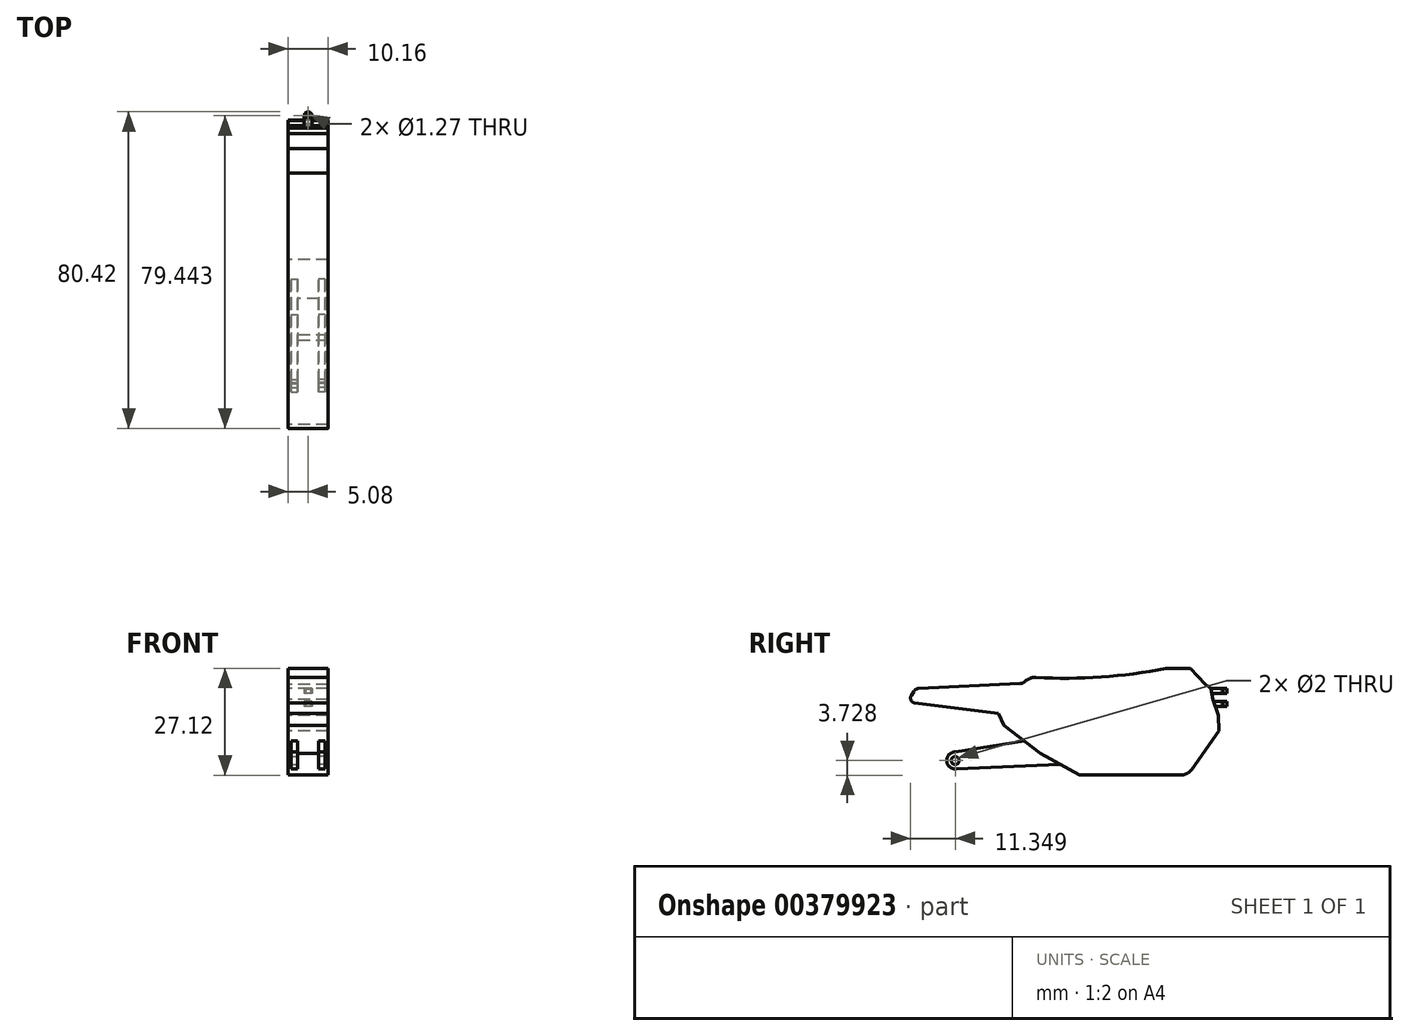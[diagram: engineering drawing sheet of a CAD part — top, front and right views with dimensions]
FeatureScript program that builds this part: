
annotation { "Feature Type Name" : "Feature", "Feature Type Description" : "" }
export const myFeature = defineFeature(function(context is Context, id is Id, definition is map)
    precondition{}
    {
        {
            var Q0;
            Q0=qCreatedBy(makeId("Right.planeOp"),FACE);
            var sketch = newSketch(context, id + "F0", { "sketchPlane" : qUnion([Q0])});
            skLineSegment(sketch, "E0", {"start": v(0.03, 4.05) * mm, "end": v(-1.34, 8.22) * mm});
            skLineSegment(sketch, "E1", {"start": v(-3.3, 12.01) * mm, "end": v(-7.13, 16.04) * mm});
            skLineSegment(sketch, "E2", {"start": v(-7.13, 16.04) * mm, "end": v(-13.37, 16.04) * mm});
            skLineSegment(sketch, "E3", {"start": v(-49.12, 12.73) * mm, "end": v(-49.2, 12.66) * mm});
            skLineSegment(sketch, "E4", {"start": v(-50.36, 12.17) * mm, "end": v(-76.22, 10.91) * mm});
            skLineSegment(sketch, "E5", {"start": v(-77.36, 10.24) * mm, "end": v(-78.02, 9.16) * mm});
            skLineSegment(sketch, "E6", {"start": v(-6.72, -9.55) * mm, "end": v(0.09, 0.2) * mm});
            skLineSegment(sketch, "E7", {"start": v(0.09, 0.2) * mm, "end": v(0.03, 4.05) * mm});
            skArc(sketch, "E8", {"start": v(-46.3, 13.76) * mm, "mid": v(-29.76, 13.87) * mm, "end": v(-13.37, 16.04) * mm});
            skPoint(sketch, "E9.visualSharp", {"position": v(-47.92, 13.86) * mm});
            skArc(sketch, "E9.filletArc", {"start": v(-46.3, 13.76) * mm, "mid": v(-47.82, 13.53) * mm, "end": v(-49.12, 12.73) * mm});
            skPoint(sketch, "E10.visualSharp", {"position": v(-78.92, 7.68) * mm});
            skArc(sketch, "E10.filletArc", {"start": v(-78.02, 9.16) * mm, "mid": v(-78.11, 8.01) * mm, "end": v(-77.24, 7.27) * mm});
            skPoint(sketch, "E11.visualSharp", {"position": v(-76.97, 10.88) * mm});
            skArc(sketch, "E11.filletArc", {"start": v(-76.22, 10.91) * mm, "mid": v(-76.88, 10.72) * mm, "end": v(-77.36, 10.24) * mm});
            skPoint(sketch, "E12.visualSharp", {"position": v(-49.69, 12.2) * mm});
            skArc(sketch, "E12.filletArc", {"start": v(-50.36, 12.17) * mm, "mid": v(-49.73, 12.31) * mm, "end": v(-49.2, 12.66) * mm});
            skPoint(sketch, "E13.visualSharp", {"position": v(-10.32, -14.7) * mm});
            skLineSegment(sketch, "E14", {"start": v(-54.53, 1.5) * mm, "end": v(-55.89, 4.57) * mm});
            skLineSegment(sketch, "E15", {"start": v(-55.89, 4.57) * mm, "end": v(-77.24, 7.27) * mm});
            skLineSegment(sketch, "E16", {"start": v(-35.32, -11.08) * mm, "end": v(-45.2, -5.51) * mm});
            skLineSegment(sketch, "E17", {"start": v(-45.2, -5.51) * mm, "end": v(-54.53, 1.5) * mm});
            skLineSegment(sketch, "E18", {"start": v(-35.32, -11.08) * mm, "end": v(-9.64, -11.08) * mm});
            skPoint(sketch, "E19.visualSharp", {"position": v(-7.79, -11.08) * mm});
            skArc(sketch, "E19.filletArc", {"start": v(-9.64, -11.08) * mm, "mid": v(-8, -10.67) * mm, "end": v(-6.72, -9.55) * mm});
            skPoint(sketch, "E20.endSnap0", {"position": v(-63.29, 11.54) * mm});
            skLineSegment(sketch, "E21", {"start": v(-49.3, -2.43) * mm, "end": v(-66.86, -5.2) * mm});
            skLineSegment(sketch, "E22", {"start": v(-66.86, -9.5) * mm, "end": v(-40.26, -8.3) * mm});
            skPoint(sketch, "E20.end.orphan", {"position": v(-63.29, -9.53) * mm});
            skPoint(sketch, "E23.end.orphan", {"position": v(-63.29, -5.99) * mm});
            skArc(sketch, "E24", {"start": v(-66.83, -5.2) * mm, "mid": v(-69.01, -7.48) * mm, "end": v(-66.58, -9.49) * mm});
            skCircle(sketch, "E25", {"center": v(-66.86, -7.35) * mm, "radius": 1 * mm});
            skLineSegment(sketch, "E26", {"start": v(-1.34, 8.22) * mm, "end": v(-1.93, 10.91) * mm});
            skLineSegment(sketch, "E27", {"start": v(-1.93, 10.91) * mm, "end": v(-3.3, 12.01) * mm});
            skPoint(sketch, "E28.orphan", {"position": v(-2.2, 10.88) * mm});
            skSolve(sketch);
        }
        {
            var Q0;
            Q0=makeQuery(id+"F0.imprint","IMPRINT",FACE,{"disambiguationData":[TD([[makeQuery(id+"F0.imprint","IMPRINT",EDGE,{"derivedFrom":sQuery(id+"F0.wireOp",EDGE,"E0")}),1.0]])]});
            extrude(context, id + "F1", {"entities" : qUnion([Q0]), "depth" : 5.08 * mm, "hasSecondDirection" : true, "secondDirectionOppositeDirection" : true, "secondDirectionDepth" : 5.08 * mm});
        }
        {
            var Q0;
            {var subQ3=sQuery(id+"F0.wireOp",EDGE,"E24");Q0=makeQuery(id+"F0.imprint","IMPRINT",FACE,{"disambiguationData":[TD([[makeQuery(id+"F0.imprint","IMPRINT",EDGE,{"derivedFrom":subQ3}),1.0]])]});}
            extrude(context, id + "F2", {"entities" : qUnion([Q0]), "depth" : 4.32 * mm, "hasSecondDirection" : true, "secondDirectionOppositeDirection" : false, "secondDirectionDepth" : 2.7 * mm});
        }
        {
            var Q0;
            Q0=makeQuery(id+"F2.opExtrude","SWEPT_BODY",BODY,{"disambiguationData":[OSD([sQuery(id+"F0.wireOp",EDGE,"E16"),sQuery(id+"F0.wireOp",EDGE,"E17"),sQuery(id+"F0.wireOp",EDGE,"E21"),sQuery(id+"F0.wireOp",EDGE,"E22"),sQuery(id+"F0.wireOp",EDGE,"E24"),sQuery(id+"F0.wireOp",EDGE,"E25")])]});
            var Q1;
            Q1=qCreatedBy(makeId("Right.planeOp"),FACE);
            mirror(context, id + "F3", {"operationType" : NewBodyOperationType.ADD, "entities" : qUnion([Q0]), "mirrorPlane" : qUnion([Q1])});
        }
        {
            var Q0;
            Q0=qCreatedBy(makeId("Top.planeOp"),FACE);
            var sketch = newSketch(context, id + "F4", { "sketchPlane" : qUnion([Q0])});
            skLineSegment(sketch, "E29", {"start": v(-0.98, -1.9) * mm, "end": v(-0.98, 1.17) * mm});
            skLineSegment(sketch, "E30.MirrorCS", {"start": v(0.98, -1.9) * mm, "end": v(0.98, 1.17) * mm});
            skLineSegment(sketch, "E31", {"start": v(-0.98, -1.9) * mm, "end": v(0.98, -1.9) * mm});
            skArc(sketch, "E32", {"start": v(0.98, 1.17) * mm, "mid": v(0, 2.21) * mm, "end": v(-0.98, 1.17) * mm});
            skPoint(sketch, "E33.orphan", {"position": v(0.98, 1.64) * mm});
            skPoint(sketch, "E34.MirrorCS.end.orphan", {"position": v(0, 1.64) * mm});
            skLineSegment(sketch, "E35", {"start": v(-0.98, 1.17) * mm, "end": v(-0.98, 1.17) * mm});
            skPoint(sketch, "E36.orphan", {"position": v(-0.98, 1.64) * mm});
            skLineSegment(sketch, "E37.MirrorCS", {"start": v(0.98, 1.17) * mm, "end": v(0.98, 1.17) * mm});
            skCircle(sketch, "E38", {"center": v(0, 1.23) * mm, "radius": 0.64 * mm});
            skSolve(sketch);
        }
        {
            var Q0;
            Q0 = qSketchRegion(id + "F4", true);
            extrude(context, id + "F5", {"entities" : qUnion([Q0]), "operationType" : NewBodyOperationType.ADD, "offsetDistance" : 25.4 * mm, "depth" : 10.92 * mm, "hasSecondDirection" : true, "secondDirectionOppositeDirection" : false, "secondDirectionDepth" : 9.65 * mm});
        }
        {
            var Q0;
            Q0 = qSketchRegion(id + "F4", true);
            extrude(context, id + "F6", {"entities" : qUnion([Q0]), "operationType" : NewBodyOperationType.ADD, "offsetDistance" : 25.4 * mm, "depth" : 7.62 * mm, "hasSecondDirection" : true, "secondDirectionOppositeDirection" : false, "secondDirectionDepth" : 6.35 * mm});
        }
    });
